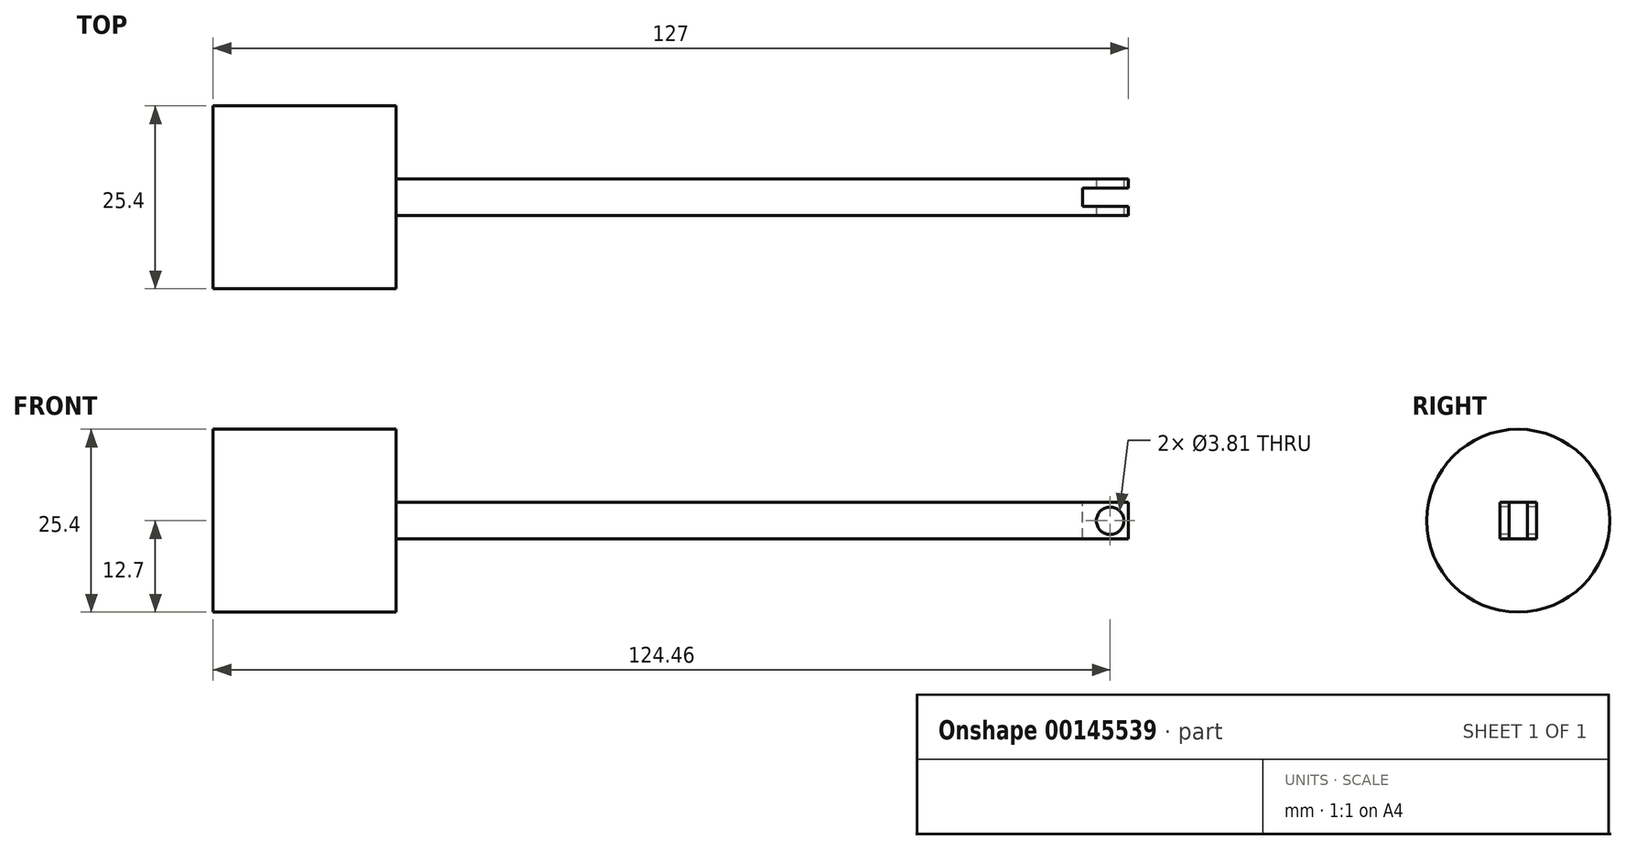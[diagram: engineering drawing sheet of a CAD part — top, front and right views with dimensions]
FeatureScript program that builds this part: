
annotation { "Feature Type Name" : "Feature", "Feature Type Description" : "" }
export const myFeature = defineFeature(function(context is Context, id is Id, definition is map)
    precondition{}
    {
        {
            var Q0;
            Q0=qCreatedBy(makeId("Right.planeOp"),FACE);
            var sketch = newSketch(context, id + "F0", { "sketchPlane" : qUnion([Q0])});
            skCircle(sketch, "E0", {"center": v(0, 0) * mm, "radius": 12.7 * mm});
            skSolve(sketch);
        }
        {
            var Q0;
            Q0 = qSketchRegion(id + "F0", true);
            extrude(context, id + "F1", {"entities" : qUnion([Q0]), "depth" : 25.4 * mm});
        }
        {
            var Q0;
            Q0=qCreatedBy(makeId("Top.planeOp"),FACE);
            var sketch = newSketch(context, id + "F2", { "sketchPlane" : qUnion([Q0])});
            skLineSegment(sketch, "E1", {"start": v(25.4, 2.54) * mm, "end": v(127, 2.54) * mm});
            skLineSegment(sketch, "E2", {"start": v(127, 2.54) * mm, "end": v(127, -2.54) * mm});
            skLineSegment(sketch, "E3", {"start": v(127, -2.54) * mm, "end": v(25.4, -2.54) * mm});
            skLineSegment(sketch, "E4", {"start": v(25.4, -2.54) * mm, "end": v(25.4, 2.54) * mm});
            skSolve(sketch);
        }
        {
            var Q0;
            Q0=makeQuery(id+"F2.imprint","IMPRINT",FACE,{"disambiguationData":[TD([[makeQuery(id+"F2.imprint","IMPRINT",EDGE,{"derivedFrom":sQuery(id+"F2.wireOp",EDGE,"E1")}),-1.0]])]});
            extrude(context, id + "F3", {"entities" : qUnion([Q0]), "operationType" : NewBodyOperationType.ADD, "endBound" : BoundingType.SYMMETRIC, "depth" : 5.08 * mm});
        }
        {
            var Q0;
            Q0=makeQuery(id+"F3.opExtrude","SWEPT_FACE",FACE,{"disambiguationData":[OSD([sQuery(id+"F2.wireOp",EDGE,"E3")])]});
            var sketch = newSketch(context, id + "F4", { "sketchPlane" : qUnion([Q0])});
            skCircle(sketch, "E5", {"center": v(124.46, 0) * mm, "radius": 1.9 * mm});
            skSolve(sketch);
        }
        {
            var Q0;
            Q0=makeQuery(id+"F4.imprint","IMPRINT",FACE,{"disambiguationData":[TD([[makeQuery(id+"F4.imprint","IMPRINT",EDGE,{"derivedFrom":sQuery(id+"F4.wireOp",EDGE,"E5")}),1.0]])]});
            extrude(context, id + "F5", {"entities" : qUnion([Q0]), "operationType" : NewBodyOperationType.REMOVE, "endBound" : BoundingType.THROUGH_ALL, "oppositeDirection" : true, "depth" : 25.4 * mm});
        }
        {
            var Q0;
            Q0=makeQuery(id+"F3.opExtrude","CAP_FACE",FACE,{"disambiguationData":[OSD([sQuery(id+"F2.wireOp",EDGE,"E1"),sQuery(id+"F2.wireOp",EDGE,"E2"),sQuery(id+"F2.wireOp",EDGE,"E3"),sQuery(id+"F2.wireOp",EDGE,"E4")])],"isStart":false});
            var sketch = newSketch(context, id + "F6", { "sketchPlane" : qUnion([Q0])});
            skLineSegment(sketch, "E6", {"start": v(127, 1.27) * mm, "end": v(120.65, 1.27) * mm});
            skLineSegment(sketch, "E7", {"start": v(120.65, 1.27) * mm, "end": v(120.65, -1.27) * mm});
            skLineSegment(sketch, "E8", {"start": v(120.65, -1.27) * mm, "end": v(127, -1.27) * mm});
            skLineSegment(sketch, "E9", {"start": v(127, -1.27) * mm, "end": v(127, 1.27) * mm});
            skSolve(sketch);
        }
        {
            var Q0;
            Q0 = qSketchRegion(id + "F6", true);
            extrude(context, id + "F7", {"entities" : qUnion([Q0]), "operationType" : NewBodyOperationType.REMOVE, "endBound" : BoundingType.THROUGH_ALL, "oppositeDirection" : true, "depth" : 25.4 * mm});
        }
    });
